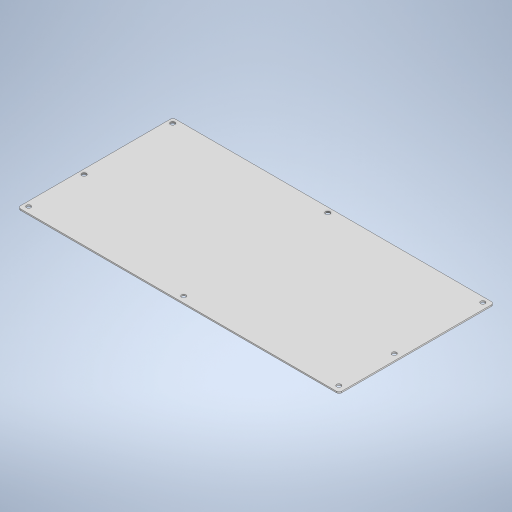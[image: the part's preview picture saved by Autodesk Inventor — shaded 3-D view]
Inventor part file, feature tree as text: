
AUTODESK INVENTOR PART (.ipt)
format: ipt  version: 2023 (Build 270158000, 158)  size: 238,592 bytes
history: native  units: in
note: dims shown in document units (in); Inventor stores cm internally (conversion verified against a paired STEP export)
features: extrude x2, sketch x2, fillet x1
ambient origin geometry x8: Origin, YZ Plane, XZ Plane, XY Plane, X Axis, Y Axis, Z Axis, Center Point
bodies: Solid1 (feature_tree)
feature tree (5):
  extrude  "Extrusion1"  Depth=14.5in
  extrude  "Extrusion2"  Depth=0.125in
  fillet  "Fillet1"  Radius=0.2in
  sketch  "Sketch1"  dims[d0=7.0in d1=14.5in]
  sketch  "Sketch2"  dims[d2=0.0625in d3=0.0in d4=0.2in d6=0.2in d8=0.2in d10=0.2in d12=0.2in d14=0.2in d16=0.2in d17=0.2in d18=1.0in d19=0.0in d20=0.125in]
